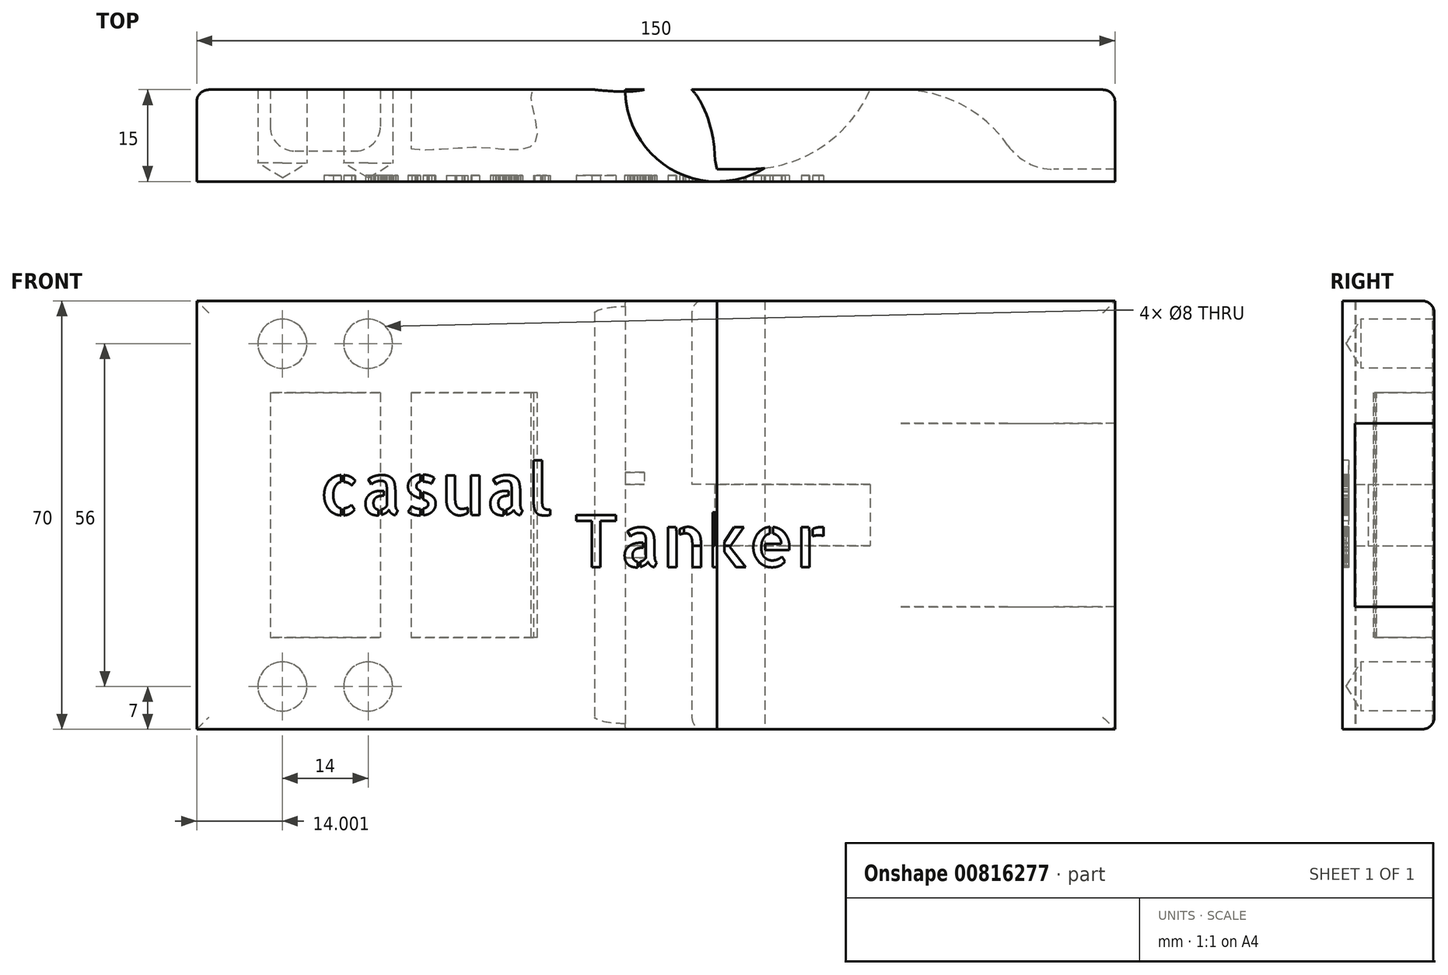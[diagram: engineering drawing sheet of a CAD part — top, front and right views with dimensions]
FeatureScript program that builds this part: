
annotation { "Feature Type Name" : "Feature", "Feature Type Description" : "" }
export const myFeature = defineFeature(function(context is Context, id is Id, definition is map)
    precondition{}
    {
        {
            var Q0;
            Q0=qCreatedBy(makeId("Top.planeOp"),FACE);
            var sketch = newSketch(context, id + "F0", { "sketchPlane" : qUnion([Q0])});
            skLineSegment(sketch, "E0.bottom", {"start": v(91.44, -7.74) * mm, "end": v(-58.56, -7.74) * mm});
            skLineSegment(sketch, "E0.top", {"start": v(91.44, 7.26) * mm, "end": v(-58.56, 7.26) * mm});
            skLineSegment(sketch, "E0.left", {"start": v(91.44, -7.74) * mm, "end": v(91.44, 7.26) * mm});
            skLineSegment(sketch, "E0.right", {"start": v(-58.56, -7.74) * mm, "end": v(-58.56, 7.26) * mm});
            skLineSegment(sketch, "E1", {"start": v(91.44, -5.74) * mm, "end": v(81.44, -5.74) * mm});
            skArc(sketch, "E2", {"start": v(81.44, -5.74) * mm, "mid": v(77.21, -4.7) * mm, "end": v(73.94, -1.84) * mm});
            skArc(sketch, "E3", {"start": v(73.94, -1.84) * mm, "mid": v(66.3, 4.85) * mm, "end": v(56.44, 7.26) * mm});
            skLineSegment(sketch, "E4", {"start": v(26.44, -5.74) * mm, "end": v(31.44, -5.74) * mm});
            skArc(sketch, "E5", {"start": v(31.44, -5.74) * mm, "mid": v(43.37, -2.2) * mm, "end": v(51.44, 7.26) * mm});
            skLineSegment(sketch, "E6", {"start": v(-58.56, -5.74) * mm, "end": v(106.76, -5.74) * mm, "construction": true});
            skFitSpline(sketch, "E7", {"points": [v(26.44, -5.74) * mm, v(25.26, -0.18) * mm, v(21.4, 5.71) * mm, v(6.44, 7.26) * mm], "startDerivative": vector(-4.01, 21.25) * mm, "endDerivative": vector(-55.89, 0) * mm});
            skLineSegment(sketch, "E8.bottom", {"start": v(-46.56, 7.26) * mm, "end": v(-28.56, 7.26) * mm});
            skLineSegment(sketch, "E8.top", {"start": v(-42.56, -2.74) * mm, "end": v(-32.56, -2.74) * mm});
            skLineSegment(sketch, "E8.left", {"start": v(-46.56, 7.26) * mm, "end": v(-46.56, 1.26) * mm});
            skLineSegment(sketch, "E8.right", {"start": v(-28.56, 7.26) * mm, "end": v(-28.56, 1.26) * mm});
            skLineSegment(sketch, "E9", {"start": v(-23.56, 7.26) * mm, "end": v(-23.56, -2.34) * mm});
            skFitSpline(sketch, "E10", {"points": [v(-23.56, -2.34) * mm, v(-16.77, -2.34) * mm, v(-10.45, -2.1) * mm, v(-4.83, 0) * mm, v(-3.56, 7.26) * mm], "startDerivative": vector(19.96, -2.18) * mm, "endDerivative": vector(3.98, 19.09) * mm});
            skPoint(sketch, "E11.visualSharp", {"position": v(-46.56, -2.74) * mm});
            skArc(sketch, "E11.filletArc", {"start": v(-46.56, 1.26) * mm, "mid": v(-45.39, -1.56) * mm, "end": v(-42.56, -2.74) * mm});
            skPoint(sketch, "E12.visualSharp", {"position": v(-28.56, -2.74) * mm});
            skArc(sketch, "E12.filletArc", {"start": v(-32.56, -2.74) * mm, "mid": v(-29.73, -1.56) * mm, "end": v(-28.56, 1.26) * mm});
            skCircle(sketch, "E13", {"center": v(26.44, 7.26) * mm, "radius": 15 * mm});
            skSolve(sketch);
        }
        {
            var Q0;
            Q0=qCreatedBy(makeId("Top.planeOp"),FACE);
            var sketch = newSketch(context, id + "F1", { "sketchPlane" : qUnion([Q0])});
            skFitSpline(sketch, "E14.0", {"points": [v(-23.56, -2.34) * mm, v(-21.87, -2.52) * mm, v(-16.45, -2.3) * mm, v(-10.78, -2.22) * mm, v(-3.3, -1.43) * mm, v(-3.9, 5.58) * mm, v(-3.56, 7.26) * mm]});
            skLineSegment(sketch, "E14.1", {"start": v(-23.56, 7.26) * mm, "end": v(-23.56, -2.34) * mm});
            skLineSegment(sketch, "E14.2", {"start": v(-28.56, 7.26) * mm, "end": v(-28.56, 1.26) * mm});
            skArc(sketch, "E14.3", {"start": v(-32.56, -2.74) * mm, "mid": v(-29.73, -1.56) * mm, "end": v(-28.56, 1.26) * mm});
            skLineSegment(sketch, "E14.4", {"start": v(-42.56, -2.74) * mm, "end": v(-32.56, -2.74) * mm});
            skArc(sketch, "E14.5", {"start": v(-46.56, 1.26) * mm, "mid": v(-45.39, -1.56) * mm, "end": v(-42.56, -2.74) * mm});
            skLineSegment(sketch, "E14.6", {"start": v(-46.56, 7.26) * mm, "end": v(-46.56, 1.26) * mm});
            skLineSegment(sketch, "E14.8", {"start": v(-58.56, -7.74) * mm, "end": v(-58.56, 7.26) * mm});
            skLineSegment(sketch, "E15", {"start": v(-58.56, -7.74) * mm, "end": v(1.44, -7.74) * mm});
            skLineSegment(sketch, "E16", {"start": v(1.44, 7.26) * mm, "end": v(-58.56, 7.26) * mm});
            skPoint(sketch, "E17.middle", {"position": v(1.44, 0) * mm});
            skFitSpline(sketch, "E18.0", {"points": [v(26.44, -5.74) * mm, v(26.08, -3.84) * mm, v(25.69, -0.2) * mm, v(21.45, 7.91) * mm, v(14.55, 7.26) * mm, v(6.44, 7.26) * mm]});
            skArc(sketch, "E18.1", {"start": v(31.44, -5.74) * mm, "mid": v(43.37, -2.2) * mm, "end": v(51.44, 7.26) * mm});
            skLineSegment(sketch, "E18.2", {"start": v(26.44, -5.74) * mm, "end": v(31.44, -5.74) * mm});
            skArc(sketch, "E18.3", {"start": v(73.94, -1.84) * mm, "mid": v(66.3, 4.85) * mm, "end": v(56.44, 7.26) * mm});
            skArc(sketch, "E18.4", {"start": v(81.44, -5.74) * mm, "mid": v(77.21, -4.7) * mm, "end": v(73.94, -1.84) * mm});
            skLineSegment(sketch, "E18.5", {"start": v(91.44, -5.74) * mm, "end": v(81.44, -5.74) * mm});
            skCircle(sketch, "E18.7", {"center": v(26.44, 7.26) * mm, "radius": 15 * mm});
            skLineSegment(sketch, "E19.bottom", {"start": v(1.44, 7.26) * mm, "end": v(91.44, 7.26) * mm});
            skLineSegment(sketch, "E19.top", {"start": v(1.44, -7.74) * mm, "end": v(91.44, -7.74) * mm});
            skLineSegment(sketch, "E19.right", {"start": v(91.44, 7.26) * mm, "end": v(91.44, -7.74) * mm});
            skSolve(sketch);
        }
        {
            var Q0;
            {var subQ5=sQuery(id+"F1.wireOp",EDGE,"E17.right");Q0=makeQuery(id+"F1.imprint","IMPRINT",FACE,{"disambiguationData":[TD([[makeQuery(id+"F1.imprint","IMPRINT",EDGE,{"derivedFrom":subQ5}),-1.0]])]});}
            var Q1;
            {var subQ6=sQuery(id+"F1.wireOp",EDGE,"E14.0");Q1=makeQuery(id+"F1.imprint","IMPRINT",FACE,{"disambiguationData":[TD([[makeQuery(id+"F1.imprint","IMPRINT",EDGE,{"derivedFrom":subQ6}),-1.0]])]});}
            var Q2;
            {var subQ0=sQuery(id+"F1.wireOp",EDGE,"E14.0");Q2=makeQuery(id+"F1.imprint","IMPRINT",FACE,{"disambiguationData":[TD([[makeQuery(id+"F1.imprint","IMPRINT",EDGE,{"derivedFrom":subQ0}),1.0]])]});}
            var Q3;
            {var subQ1=sQuery(id+"F1.wireOp",EDGE,"E14.2");Q3=makeQuery(id+"F1.imprint","IMPRINT",FACE,{"disambiguationData":[TD([[makeQuery(id+"F1.imprint","IMPRINT",EDGE,{"derivedFrom":subQ1}),-1.0]])]});}
            var Q4;
            {var subQ5=sQuery(id+"F1.wireOp",EDGE,"bb9fbce9-dafe-4efa-a9e3-36aaa79ced1d.1");Q4=makeQuery(id+"F1.imprint","IMPRINT",FACE,{"disambiguationData":[TD([[makeQuery(id+"F1.imprint","IMPRINT",EDGE,{"derivedFrom":subQ5}),-1.0]])]});}
            var Q5;
            {var subQ1=sQuery(id+"F1.wireOp",EDGE,"E14.1");Q5=makeQuery(id+"F1.imprint","IMPRINT",FACE,{"disambiguationData":[TD([[makeQuery(id+"F1.imprint","IMPRINT",EDGE,{"derivedFrom":subQ1}),-1.0]])]});}
            var Q6;
            {var subQ1=sQuery(id+"F1.wireOp",EDGE,"bb9fbce9-dafe-4efa-a9e3-36aaa79ced1d.1");var subQ3=sQuery(id+"F1.wireOp",EDGE,"E14.0");var subQ4=makeQuery(id+"F1.imprint","INTERSECT",VERTEX,{"derivedFrom":[subQ3,subQ1]});Q6=makeQuery(id+"F1.imprint","IMPRINT",FACE,{"disambiguationData":[TD([[makeQuery(id+"F1.imprint","IMPRINT",EDGE,{"disambiguationData":[TD([[subQ4,-1.0]])],"derivedFrom":subQ3}),-1.0]])]});}
            extrude(context, id + "F2", {"entities" : qUnion([Q0, Q1, Q2, Q3, Q4, Q5, Q6]), "depth" : 70 * mm, "offsetDistance" : 25 * mm, "symmetric" : true});
        }
        {
            var Q0;
            {var subQ1=sQuery(id+"F1.wireOp",EDGE,"E14.2");Q0=makeQuery(id+"F1.imprint","IMPRINT",FACE,{"disambiguationData":[TD([[makeQuery(id+"F1.imprint","IMPRINT",EDGE,{"derivedFrom":subQ1}),-1.0]])]});}
            var Q1;
            {var subQ0=sQuery(id+"F1.wireOp",EDGE,"E14.0");Q1=makeQuery(id+"F1.imprint","IMPRINT",FACE,{"disambiguationData":[TD([[makeQuery(id+"F1.imprint","IMPRINT",EDGE,{"derivedFrom":subQ0}),1.0]])]});}
            extrude(context, id + "F3", {"entities" : qUnion([Q0, Q1]), "operationType" : NewBodyOperationType.REMOVE, "depth" : 40 * mm, "offsetDistance" : 25 * mm, "symmetric" : true});
        }
        {
            var Q0;
            {var subQ4=sQuery(id+"F1.wireOp",EDGE,"E17.left");Q0=makeQuery(id+"F1.imprint","IMPRINT",FACE,{"disambiguationData":[TD([[makeQuery(id+"F1.imprint","IMPRINT",EDGE,{"derivedFrom":subQ4}),-1.0]])]});}
            var Q1;
            {var subQ0=sQuery(id+"F1.wireOp",EDGE,"E17.left");Q1=makeQuery(id+"F1.imprint","IMPRINT",FACE,{"disambiguationData":[TD([[makeQuery(id+"F1.imprint","IMPRINT",EDGE,{"derivedFrom":subQ0}),1.0]])]});}
            var Q2;
            {var subQ4=sQuery(id+"F1.wireOp",EDGE,"E18.3");Q2=makeQuery(id+"F1.imprint","IMPRINT",FACE,{"disambiguationData":[TD([[makeQuery(id+"F1.imprint","IMPRINT",EDGE,{"derivedFrom":subQ4}),1.0]])]});}
            var Q3;
            {var subQ1=sQuery(id+"F1.wireOp",EDGE,"E18.3");Q3=makeQuery(id+"F1.imprint","IMPRINT",FACE,{"disambiguationData":[TD([[makeQuery(id+"F1.imprint","IMPRINT",EDGE,{"derivedFrom":subQ1}),-1.0]])]});}
            var Q4;
            {var subQ0=sQuery(id+"F1.wireOp",EDGE,"E19.bottom");var subQ1=sQuery(id+"F1.wireOp",EDGE,"E18.1");var subQ2=makeQuery(id+"F1.imprint","INTERSECT",VERTEX,{"derivedFrom":[subQ1,subQ0]});Q4=makeQuery(id+"F1.imprint","IMPRINT",FACE,{"disambiguationData":[TD([[makeQuery(id+"F1.imprint","IMPRINT",EDGE,{"disambiguationData":[TD([[subQ2,1.0]])],"derivedFrom":subQ1}),1.0]])]});}
            var Q5;
            {var subQ4=sQuery(id+"F1.wireOp",EDGE,"E18.2");Q5=makeQuery(id+"F1.imprint","IMPRINT",FACE,{"disambiguationData":[TD([[makeQuery(id+"F1.imprint","IMPRINT",EDGE,{"derivedFrom":subQ4}),-1.0]])]});}
            var Q6;
            {var subQ5=sQuery(id+"F1.wireOp",EDGE,"E18.2");Q6=makeQuery(id+"F1.imprint","IMPRINT",FACE,{"disambiguationData":[TD([[makeQuery(id+"F1.imprint","IMPRINT",EDGE,{"derivedFrom":subQ5}),1.0]])]});}
            extrude(context, id + "F4", {"entities" : qUnion([Q0, Q1, Q2, Q3, Q4, Q5, Q6]), "operationType" : NewBodyOperationType.ADD, "depth" : 70 * mm, "offsetDistance" : 25 * mm, "symmetric" : true});
        }
        {
            var Q0;
            {var subQ0=sQuery(id+"F1.wireOp",EDGE,"E18.7");var subQ1=sQuery(id+"F1.wireOp",EDGE,"E18.0");var subQ2=makeQuery(id+"F1.imprint","INTERSECT",VERTEX,{"derivedFrom":[subQ1,subQ0]});Q0=makeQuery(id+"F1.imprint","IMPRINT",FACE,{"disambiguationData":[TD([[makeQuery(id+"F1.imprint","IMPRINT",EDGE,{"disambiguationData":[TD([[subQ2,1.0]])],"derivedFrom":subQ1}),-1.0]])]});}
            extrude(context, id + "F5", {"entities" : qUnion([Q0]), "operationType" : NewBodyOperationType.ADD, "depth" : 14 * mm, "offsetDistance" : 25 * mm, "symmetric" : true});
        }
        {
            var Q0;
            {var subQ0=sQuery(id+"F1.wireOp",EDGE,"E18.7");var subQ1=sQuery(id+"F1.wireOp",EDGE,"E18.0");var subQ2=makeQuery(id+"F1.imprint","INTERSECT",VERTEX,{"disambiguationData":[OD(0.0)],"derivedFrom":[subQ1,subQ0]});Q0=makeQuery(id+"F1.imprint","IMPRINT",FACE,{"disambiguationData":[TD([[makeQuery(id+"F1.imprint","IMPRINT",EDGE,{"disambiguationData":[TD([[subQ2,1.0]])],"derivedFrom":subQ1}),-1.0]])]});}
            var Q1;
            {var subQ1=sQuery(id+"F0.wireOp",EDGE,"E4");Q1=makeQuery(id+"F0.imprint","IMPRINT",FACE,{"disambiguationData":[TD([[makeQuery(id+"F0.imprint","IMPRINT",EDGE,{"derivedFrom":subQ1}),1.0]])]});}
            var Q2;
            {var subQ0=sQuery(id+"F0.wireOp",EDGE,"E5");var subQ1=sQuery(id+"F0.wireOp",EDGE,"E0.top");var subQ2=makeQuery(id+"F0.imprint","INTERSECT",VERTEX,{"derivedFrom":[subQ1,subQ0]});Q2=makeQuery(id+"F0.imprint","IMPRINT",FACE,{"disambiguationData":[TD([[makeQuery(id+"F0.imprint","IMPRINT",EDGE,{"disambiguationData":[TD([[subQ2,-1.0]])],"derivedFrom":subQ1}),1.0]])]});}
            extrude(context, id + "F6", {"entities" : qUnion([Q0, Q1, Q2]), "operationType" : NewBodyOperationType.REMOVE, "depth" : 10 * mm, "offsetDistance" : 25 * mm, "symmetric" : true});
        }
        {
            var Q0;
            {var subQ0=sQuery(id+"F1.wireOp",EDGE,"E18.7");var subQ1=sQuery(id+"F1.wireOp",EDGE,"E18.0");var subQ2=makeQuery(id+"F1.imprint","INTERSECT",VERTEX,{"disambiguationData":[OD(1.0)],"derivedFrom":[subQ1,subQ0]});Q0=makeQuery(id+"F1.imprint","IMPRINT",FACE,{"disambiguationData":[TD([[makeQuery(id+"F1.imprint","IMPRINT",EDGE,{"disambiguationData":[TD([[subQ2,-1.0]])],"derivedFrom":subQ1}),-1.0]])]});}
            var Q1;
            {var subQ5=sQuery(id+"F1.wireOp",EDGE,"E18.1");Q1=makeQuery(id+"F1.imprint","IMPRINT",FACE,{"disambiguationData":[TD([[makeQuery(id+"F1.imprint","IMPRINT",EDGE,{"derivedFrom":subQ5}),1.0]])]});}
            extrude(context, id + "F7", {"entities" : qUnion([Q0, Q1]), "operationType" : NewBodyOperationType.REMOVE, "oppositeDirection" : true, "depth" : 10 * mm, "offsetDistance" : 25 * mm, "symmetric" : true});
        }
        {
            var Q0;
            {var subQ1=sQuery(id+"F1.wireOp",EDGE,"E18.3");Q0=makeQuery(id+"F1.imprint","IMPRINT",FACE,{"disambiguationData":[TD([[makeQuery(id+"F1.imprint","IMPRINT",EDGE,{"derivedFrom":subQ1}),-1.0]])]});}
            extrude(context, id + "F8", {"entities" : qUnion([Q0]), "operationType" : NewBodyOperationType.REMOVE, "depth" : 30 * mm, "offsetDistance" : 25 * mm, "symmetric" : true});
        }
        {
            var Q0;
            {var subQ0=sQuery(id+"F1.wireOp",EDGE,"E19.bottom");var subQ1=makeQuery(id+"F1.imprint","INTERSECT",VERTEX,{"derivedFrom":[sQuery(id+"F1.wireOp",EDGE,"E18.3"),subQ0]});var subQ2=makeQuery(id+"F1.imprint","INTERSECT",VERTEX,{"derivedFrom":[sQuery(id+"F1.wireOp",EDGE,"E18.1"),subQ0]});var subQ3=sQuery(id+"F1.wireOp",EDGE,"E18.7");var subQ4=makeQuery(id+"F1.imprint","INTERSECT",VERTEX,{"disambiguationData":[OD(0.0)],"derivedFrom":[subQ3,subQ0]});var subQ5=sQuery(id+"F1.wireOp",EDGE,"E18.0");var subQ6=makeQuery(id+"F1.imprint","INTERSECT",VERTEX,{"disambiguationData":[OD(1.0)],"derivedFrom":[subQ5,subQ0]});var subQ8=makeQuery(id+"F1.imprint","INTERSECT",VERTEX,{"disambiguationData":[OD(0.0)],"derivedFrom":[subQ5,subQ0]});Q0=makeQuery(id+"Fk8vee3glepebii_2.boolean.opBoolean","MERGE",EDGE,{"derivedFrom":[makeQuery(id+"F4.opExtrude","CAP_EDGE",EDGE,{"disambiguationData":[OSD([subQ0]),TDD([makeQuery(id+"F1.imprint","IMPRINT",EDGE,{"disambiguationData":[TD([[subQ8,1.0]])],"derivedFrom":subQ0}),makeQuery(id+"F1.imprint","IMPRINT",EDGE,{"disambiguationData":[TD([[subQ8,-1.0]])],"derivedFrom":subQ0})])],"isStart":false}),makeQuery(id+"F4.opExtrude","CAP_EDGE",EDGE,{"disambiguationData":[OSD([subQ0]),TDD([makeQuery(id+"F1.imprint","IMPRINT",EDGE,{"disambiguationData":[TD([[subQ2,-1.0]])],"derivedFrom":subQ0})])],"isStart":false}),makeQuery(id+"Fk8vee3glepebii_2.opExtrude","CAP_EDGE",EDGE,{"disambiguationData":[OSD([subQ0]),TDD([makeQuery(id+"F1.imprint","IMPRINT",EDGE,{"disambiguationData":[TD([[subQ6,1.0]])],"derivedFrom":subQ0}),makeQuery(id+"F1.imprint","IMPRINT",EDGE,{"disambiguationData":[TD([[subQ4,1.0]])],"derivedFrom":subQ0}),makeQuery(id+"F1.imprint","IMPRINT",EDGE,{"disambiguationData":[TD([[subQ2,1.0]])],"derivedFrom":subQ0})])],"isStart":false}),makeQuery(id+"Fk8vee3glepebii_2.opExtrude","CAP_EDGE",EDGE,{"disambiguationData":[OSD([subQ0]),TDD([makeQuery(id+"F1.imprint","IMPRINT",EDGE,{"disambiguationData":[TD([[subQ1,-1.0]])],"derivedFrom":subQ0})])],"isStart":false})]});}
            var Q1;
            {var subQ0=sQuery(id+"F1.wireOp",EDGE,"E19.bottom");var subQ3=sQuery(id+"F1.wireOp",EDGE,"E19.right");var subQ4=sQuery(id+"F1.wireOp",EDGE,"E18.1");var subQ6=sQuery(id+"F1.wireOp",EDGE,"E18.7");var subQ8=sQuery(id+"F1.wireOp",EDGE,"E18.0");var subQ13=sQuery(id+"F1.wireOp",EDGE,"E18.2");Q1=makeQuery(id+"F8.boolean.opBoolean","SPLIT",EDGE,{"disambiguationData":[TD([makeQuery(id+"Fk8vee3glepebii_2.opExtrude","CAP_FACE",FACE,{"disambiguationData":[OSD([subQ8,subQ4,subQ13,subQ6,subQ0])],"isStart":false})])],"derivedFrom":makeQuery(id+"Fk8vee3glepebii_2.opExtrude","SWEPT_EDGE",EDGE,{"disambiguationData":[OSD([subQ0,subQ3])]})});}
            var Q2;
            {var subQ0=sQuery(id+"F1.wireOp",EDGE,"E19.right");var subQ1=sQuery(id+"F1.wireOp",EDGE,"E19.bottom");var subQ2=sQuery(id+"F1.wireOp",EDGE,"E18.1");var subQ4=sQuery(id+"F1.wireOp",EDGE,"E18.7");var subQ6=sQuery(id+"F1.wireOp",EDGE,"E18.0");var subQ11=sQuery(id+"F1.wireOp",EDGE,"E18.2");Q2=makeQuery(id+"F8.boolean.opBoolean","SPLIT",EDGE,{"disambiguationData":[TD([makeQuery(id+"Fk8vee3glepebii_2.opExtrude","CAP_FACE",FACE,{"disambiguationData":[OSD([subQ6,subQ2,subQ11,subQ4,subQ1])],"isStart":true})])],"derivedFrom":makeQuery(id+"Fk8vee3glepebii_2.opExtrude","SWEPT_EDGE",EDGE,{"disambiguationData":[OSD([subQ1,subQ0])]})});}
            var Q3;
            {var subQ0=sQuery(id+"F1.wireOp",EDGE,"E19.bottom");var subQ1=makeQuery(id+"F1.imprint","INTERSECT",VERTEX,{"derivedFrom":[sQuery(id+"F1.wireOp",EDGE,"E18.3"),subQ0]});var subQ2=makeQuery(id+"F1.imprint","INTERSECT",VERTEX,{"derivedFrom":[sQuery(id+"F1.wireOp",EDGE,"E18.1"),subQ0]});var subQ3=sQuery(id+"F1.wireOp",EDGE,"E18.7");var subQ4=makeQuery(id+"F1.imprint","INTERSECT",VERTEX,{"disambiguationData":[OD(0.0)],"derivedFrom":[subQ3,subQ0]});var subQ5=sQuery(id+"F1.wireOp",EDGE,"E18.0");var subQ6=makeQuery(id+"F1.imprint","INTERSECT",VERTEX,{"disambiguationData":[OD(1.0)],"derivedFrom":[subQ5,subQ0]});var subQ8=makeQuery(id+"F1.imprint","INTERSECT",VERTEX,{"disambiguationData":[OD(0.0)],"derivedFrom":[subQ5,subQ0]});Q3=makeQuery(id+"Fk8vee3glepebii_2.boolean.opBoolean","MERGE",EDGE,{"derivedFrom":[makeQuery(id+"F4.opExtrude","CAP_EDGE",EDGE,{"disambiguationData":[OSD([subQ0]),TDD([makeQuery(id+"F1.imprint","IMPRINT",EDGE,{"disambiguationData":[TD([[subQ8,1.0]])],"derivedFrom":subQ0}),makeQuery(id+"F1.imprint","IMPRINT",EDGE,{"disambiguationData":[TD([[subQ8,-1.0]])],"derivedFrom":subQ0})])],"isStart":true}),makeQuery(id+"F4.opExtrude","CAP_EDGE",EDGE,{"disambiguationData":[OSD([subQ0]),TDD([makeQuery(id+"F1.imprint","IMPRINT",EDGE,{"disambiguationData":[TD([[subQ2,-1.0]])],"derivedFrom":subQ0})])],"isStart":true}),makeQuery(id+"Fk8vee3glepebii_2.opExtrude","CAP_EDGE",EDGE,{"disambiguationData":[OSD([subQ0]),TDD([makeQuery(id+"F1.imprint","IMPRINT",EDGE,{"disambiguationData":[TD([[subQ6,1.0]])],"derivedFrom":subQ0}),makeQuery(id+"F1.imprint","IMPRINT",EDGE,{"disambiguationData":[TD([[subQ4,1.0]])],"derivedFrom":subQ0}),makeQuery(id+"F1.imprint","IMPRINT",EDGE,{"disambiguationData":[TD([[subQ2,1.0]])],"derivedFrom":subQ0})])],"isStart":true}),makeQuery(id+"Fk8vee3glepebii_2.opExtrude","CAP_EDGE",EDGE,{"disambiguationData":[OSD([subQ0]),TDD([makeQuery(id+"F1.imprint","IMPRINT",EDGE,{"disambiguationData":[TD([[subQ1,-1.0]])],"derivedFrom":subQ0})])],"isStart":true})]});}
            var Q4;
            Q4=makeQuery(id+"F2.opExtrude","CAP_EDGE",EDGE,{"disambiguationData":[OSD([sQuery(id+"F1.wireOp",EDGE,"E16")])],"isStart":false});
            var Q5;
            Q5=makeQuery(id+"F2.opExtrude","SWEPT_EDGE",EDGE,{"disambiguationData":[OSD([sQuery(id+"F1.wireOp",EDGE,"E14.8"),sQuery(id+"F1.wireOp",EDGE,"E16")])]});
            var Q6;
            Q6=makeQuery(id+"F2.opExtrude","CAP_EDGE",EDGE,{"disambiguationData":[OSD([sQuery(id+"F1.wireOp",EDGE,"E16")])],"isStart":true});
            var Q7;
            Q7=makeQuery(id+"F3.boolean.opBoolean","COPY",EDGE,{"derivedFrom":makeQuery(id+"F3.opExtrude","SWEPT_EDGE",EDGE,{"disambiguationData":[OSD([sQuery(id+"F1.wireOp",EDGE,"E14.6"),sQuery(id+"F1.wireOp",EDGE,"E16")])]})});
            var Q8;
            Q8=makeQuery(id+"F3.boolean.opBoolean","COPY",EDGE,{"derivedFrom":makeQuery(id+"F3.opExtrude","SWEPT_EDGE",EDGE,{"disambiguationData":[OSD([sQuery(id+"F1.wireOp",EDGE,"E14.2"),sQuery(id+"F1.wireOp",EDGE,"E16")])]})});
            var Q9;
            Q9=makeQuery(id+"F3.boolean.opBoolean","COPY",EDGE,{"derivedFrom":makeQuery(id+"F3.opExtrude","SWEPT_EDGE",EDGE,{"disambiguationData":[OSD([sQuery(id+"F1.wireOp",EDGE,"E14.1"),sQuery(id+"F1.wireOp",EDGE,"E16")])]})});
            var Q10;
            {var subQ0=sQuery(id+"F1.wireOp",EDGE,"E16");Q10=makeQuery(id+"F3.boolean.opBoolean","COPY",EDGE,{"derivedFrom":makeQuery(id+"F3.opExtrude","CAP_EDGE",EDGE,{"disambiguationData":[OSD([subQ0]),TDD([makeQuery(id+"F1.imprint","IMPRINT",EDGE,{"disambiguationData":[TD([[makeQuery(id+"F1.imprint","INTERSECT",VERTEX,{"derivedFrom":[sQuery(id+"F1.wireOp",EDGE,"E14.2"),subQ0]}),-1.0]])],"derivedFrom":subQ0})])],"isStart":true})});}
            var Q11;
            {var subQ0=sQuery(id+"F1.wireOp",EDGE,"E16");Q11=makeQuery(id+"F3.boolean.opBoolean","COPY",EDGE,{"derivedFrom":makeQuery(id+"F3.opExtrude","CAP_EDGE",EDGE,{"disambiguationData":[OSD([subQ0]),TDD([makeQuery(id+"F1.imprint","IMPRINT",EDGE,{"disambiguationData":[TD([[makeQuery(id+"F1.imprint","INTERSECT",VERTEX,{"derivedFrom":[sQuery(id+"F1.wireOp",EDGE,"E14.2"),subQ0]}),-1.0]])],"derivedFrom":subQ0})])],"isStart":false})});}
            var Q12;
            {var subQ0=sQuery(id+"F1.wireOp",EDGE,"E19.bottom");var subQ2=sQuery(id+"F1.wireOp",EDGE,"E19.right");var subQ3=sQuery(id+"F1.wireOp",EDGE,"E19.top");var subQ4=sQuery(id+"F1.wireOp",EDGE,"E18.7");Q12=makeQuery(id+"F8.boolean.opBoolean","SPLIT",EDGE,{"disambiguationData":[TD([makeQuery(id+"F4.opExtrude","CAP_FACE",FACE,{"disambiguationData":[OSD([subQ4,subQ0,subQ3,subQ2])],"isStart":false})])],"derivedFrom":makeQuery(id+"F4.opExtrude","SWEPT_EDGE",EDGE,{"disambiguationData":[OSD([subQ0,subQ2])]})});}
            var Q13;
            {var subQ0=sQuery(id+"F1.wireOp",EDGE,"E19.right");var subQ1=sQuery(id+"F1.wireOp",EDGE,"E19.top");var subQ2=sQuery(id+"F1.wireOp",EDGE,"E19.bottom");var subQ3=sQuery(id+"F1.wireOp",EDGE,"E18.7");Q13=makeQuery(id+"F8.boolean.opBoolean","SPLIT",EDGE,{"disambiguationData":[TD([makeQuery(id+"F4.opExtrude","CAP_FACE",FACE,{"disambiguationData":[OSD([subQ3,subQ2,subQ1,subQ0])],"isStart":true})])],"derivedFrom":makeQuery(id+"F4.opExtrude","SWEPT_EDGE",EDGE,{"disambiguationData":[OSD([subQ2,subQ0])]})});}
            fillet(context, id + "F9", {"entities" : qUnion([Q0, Q1, Q2, Q3, Q4, Q5, Q6, Q7, Q8, Q9, Q10, Q11, Q12, Q13]), "radius" : 2 * mm, "tangentPropagation" : true, "allowEdgeOverflow" : false});
        }
        {
            var Q0;
            {var subQ0=sQuery(id+"F1.wireOp",EDGE,"E19.top");Q0=makeQuery(id+"F4.boolean.opBoolean","MERGE",FACE,{"derivedFrom":[makeQuery(id+"F2.opExtrude","SWEPT_FACE",FACE,{"disambiguationData":[OSD([sQuery(id+"F1.wireOp",EDGE,"E15"),subQ0])]}),makeQuery(id+"F4.opExtrude","SWEPT_FACE",FACE,{"disambiguationData":[OSD([subQ0])]})]});}
            var sketch = newSketch(context, id + "F10", { "sketchPlane" : qUnion([Q0])});
            skText(sketch, "E20", { "text": "casual", "fontName": "AllertaStencil-Regular.ttf"});
            skText(sketch, "E21", { "text": "Tanker", "fontName": "AllertaStencil-Regular.ttf"});
            skLineSegment(sketch, "E22", {"start": v(-53.13, 0) * mm, "end": v(83.14, 0) * mm, "construction": true});
            skPoint(sketch, "E23.0", {"position": v(0, 0) * mm});
            const initialGuessF10  = {"E20": [-0.03855, 0, 1, 0, 0.0085], "E21": [0.00288, -0.0085, 1, 0, 0.0085]};
            skSetInitialGuess(sketch, initialGuessF10);
            skSolve(sketch);
        }
        {
            var Q0;
            Q0=makeQuery(id+"F10.imprint","IMPRINT",FACE,{"disambiguationData":[TD([[makeQuery(id+"F10.imprint","IMPRINT",EDGE,{"derivedFrom":sQuery(id+"F10.wireOp",EDGE,"E20.sketch_text.stroke-11")}),-1.0]])]});
            var Q1;
            Q1=makeQuery(id+"F10.imprint","IMPRINT",FACE,{"disambiguationData":[TD([[makeQuery(id+"F10.imprint","IMPRINT",EDGE,{"derivedFrom":sQuery(id+"F10.wireOp",EDGE,"E20.sketch_text.stroke-0")}),-1.0]])]});
            var Q2;
            Q2=makeQuery(id+"F10.imprint","IMPRINT",FACE,{"disambiguationData":[TD([[makeQuery(id+"F10.imprint","IMPRINT",EDGE,{"derivedFrom":sQuery(id+"F10.wireOp",EDGE,"E20.sketch_text.stroke-5")}),-1.0]])]});
            var Q3;
            Q3=makeQuery(id+"F10.imprint","IMPRINT",FACE,{"disambiguationData":[TD([[makeQuery(id+"F10.imprint","IMPRINT",EDGE,{"derivedFrom":sQuery(id+"F10.wireOp",EDGE,"E20.sketch_text.stroke-29")}),-1.0]])]});
            var Q4;
            Q4=makeQuery(id+"F10.imprint","IMPRINT",FACE,{"disambiguationData":[TD([[makeQuery(id+"F10.imprint","IMPRINT",EDGE,{"derivedFrom":sQuery(id+"F10.wireOp",EDGE,"E20.sketch_text.stroke-48")}),-1.0]])]});
            var Q5;
            Q5=makeQuery(id+"F10.imprint","IMPRINT",FACE,{"disambiguationData":[TD([[makeQuery(id+"F10.imprint","IMPRINT",EDGE,{"derivedFrom":sQuery(id+"F10.wireOp",EDGE,"E20.sketch_text.stroke-84")}),-1.0]])]});
            var Q6;
            Q6=makeQuery(id+"F10.imprint","IMPRINT",FACE,{"disambiguationData":[TD([[makeQuery(id+"F10.imprint","IMPRINT",EDGE,{"derivedFrom":sQuery(id+"F10.wireOp",EDGE,"E20.sketch_text.stroke-98")}),-1.0]])]});
            var Q7;
            Q7=makeQuery(id+"F10.imprint","IMPRINT",FACE,{"disambiguationData":[TD([[makeQuery(id+"F10.imprint","IMPRINT",EDGE,{"derivedFrom":sQuery(id+"F10.wireOp",EDGE,"E20.sketch_text.stroke-113")}),-1.0]])]});
            var Q8;
            Q8=makeQuery(id+"F10.imprint","IMPRINT",FACE,{"disambiguationData":[TD([[makeQuery(id+"F10.imprint","IMPRINT",EDGE,{"derivedFrom":sQuery(id+"F10.wireOp",EDGE,"E20.sketch_text.stroke-104")}),-1.0]])]});
            var Q9;
            Q9=makeQuery(id+"F10.imprint","IMPRINT",FACE,{"disambiguationData":[TD([[makeQuery(id+"F10.imprint","IMPRINT",EDGE,{"derivedFrom":sQuery(id+"F10.wireOp",EDGE,"E20.sketch_text.stroke-127")}),-1.0]])]});
            var Q10;
            Q10=makeQuery(id+"F10.imprint","IMPRINT",FACE,{"disambiguationData":[TD([[makeQuery(id+"F10.imprint","IMPRINT",EDGE,{"derivedFrom":sQuery(id+"F10.wireOp",EDGE,"E20.sketch_text.stroke-147")}),-1.0]])]});
            var Q11;
            Q11=makeQuery(id+"F10.imprint","IMPRINT",FACE,{"disambiguationData":[TD([[makeQuery(id+"F10.imprint","IMPRINT",EDGE,{"derivedFrom":sQuery(id+"F10.wireOp",EDGE,"E20.sketch_text.stroke-152")}),-1.0]])]});
            var Q12;
            Q12=makeQuery(id+"F10.imprint","IMPRINT",FACE,{"disambiguationData":[TD([[makeQuery(id+"F10.imprint","IMPRINT",EDGE,{"derivedFrom":sQuery(id+"F10.wireOp",EDGE,"E20.sketch_text.stroke-171")}),-1.0]])]});
            var Q13;
            Q13=makeQuery(id+"F10.imprint","IMPRINT",FACE,{"disambiguationData":[TD([[makeQuery(id+"F10.imprint","IMPRINT",EDGE,{"derivedFrom":sQuery(id+"F10.wireOp",EDGE,"E20.sketch_text.stroke-207")}),-1.0]])]});
            var Q14;
            Q14=makeQuery(id+"F10.imprint","IMPRINT",FACE,{"disambiguationData":[TD([[makeQuery(id+"F10.imprint","IMPRINT",EDGE,{"derivedFrom":sQuery(id+"F10.wireOp",EDGE,"E20.sketch_text.stroke-12")}),-1.0]])]});
            extrude(context, id + "F11", {"entities" : qUnion([Q0, Q1, Q2, Q3, Q4, Q5, Q6, Q7, Q8, Q9, Q10, Q11, Q12, Q13, Q14]), "operationType" : NewBodyOperationType.REMOVE, "oppositeDirection" : true, "depth" : 1 * mm, "offsetDistance" : 25 * mm});
        }
        {
            var Q0;
            Q0=makeQuery(id+"F10.imprint","IMPRINT",FACE,{"disambiguationData":[TD([[makeQuery(id+"F10.imprint","IMPRINT",EDGE,{"derivedFrom":sQuery(id+"F10.wireOp",EDGE,"E21.sketch_text.stroke-0")}),-1.0]])]});
            var Q1;
            Q1=makeQuery(id+"F10.imprint","IMPRINT",FACE,{"disambiguationData":[TD([[makeQuery(id+"F10.imprint","IMPRINT",EDGE,{"derivedFrom":sQuery(id+"F10.wireOp",EDGE,"E21.sketch_text.stroke-8")}),-1.0]])]});
            var Q2;
            Q2=makeQuery(id+"F10.imprint","IMPRINT",FACE,{"disambiguationData":[TD([[makeQuery(id+"F10.imprint","IMPRINT",EDGE,{"derivedFrom":sQuery(id+"F10.wireOp",EDGE,"E21.sketch_text.stroke-27")}),-1.0]])]});
            var Q3;
            Q3=makeQuery(id+"F10.imprint","IMPRINT",FACE,{"disambiguationData":[TD([[makeQuery(id+"F10.imprint","IMPRINT",EDGE,{"derivedFrom":sQuery(id+"F10.wireOp",EDGE,"E21.sketch_text.stroke-63")}),-1.0]])]});
            var Q4;
            Q4=makeQuery(id+"F10.imprint","IMPRINT",FACE,{"disambiguationData":[TD([[makeQuery(id+"F10.imprint","IMPRINT",EDGE,{"derivedFrom":sQuery(id+"F10.wireOp",EDGE,"E21.sketch_text.stroke-68")}),-1.0]])]});
            var Q5;
            Q5=makeQuery(id+"F10.imprint","IMPRINT",FACE,{"disambiguationData":[TD([[makeQuery(id+"F10.imprint","IMPRINT",EDGE,{"derivedFrom":sQuery(id+"F10.wireOp",EDGE,"E21.sketch_text.stroke-94")}),-1.0]])]});
            var Q6;
            Q6=makeQuery(id+"F10.imprint","IMPRINT",FACE,{"disambiguationData":[TD([[makeQuery(id+"F10.imprint","IMPRINT",EDGE,{"derivedFrom":sQuery(id+"F10.wireOp",EDGE,"E21.sketch_text.stroke-87")}),-1.0]])]});
            var Q7;
            Q7=makeQuery(id+"F10.imprint","IMPRINT",FACE,{"disambiguationData":[TD([[makeQuery(id+"F10.imprint","IMPRINT",EDGE,{"derivedFrom":sQuery(id+"F10.wireOp",EDGE,"E21.sketch_text.stroke-111")}),-1.0]])]});
            var Q8;
            Q8=makeQuery(id+"F10.imprint","IMPRINT",FACE,{"disambiguationData":[TD([[makeQuery(id+"F10.imprint","IMPRINT",EDGE,{"derivedFrom":sQuery(id+"F10.wireOp",EDGE,"E21.sketch_text.stroke-98")}),-1.0]])]});
            var Q9;
            Q9=makeQuery(id+"F10.imprint","IMPRINT",FACE,{"disambiguationData":[TD([[makeQuery(id+"F10.imprint","IMPRINT",EDGE,{"derivedFrom":sQuery(id+"F10.wireOp",EDGE,"E21.sketch_text.stroke-135")}),-1.0]])]});
            var Q10;
            Q10=makeQuery(id+"F10.imprint","IMPRINT",FACE,{"disambiguationData":[TD([[makeQuery(id+"F10.imprint","IMPRINT",EDGE,{"derivedFrom":sQuery(id+"F10.wireOp",EDGE,"E21.sketch_text.stroke-142")}),-1.0]])]});
            extrude(context, id + "F12", {"entities" : qUnion([Q0, Q1, Q2, Q3, Q4, Q5, Q6, Q7, Q8, Q9, Q10]), "operationType" : NewBodyOperationType.REMOVE, "oppositeDirection" : true, "depth" : 1 * mm, "offsetDistance" : 25 * mm});
        }
        {
            var Q0;
            Q0=makeQuery(id+"F2.opExtrude","SWEPT_FACE",FACE,{"disambiguationData":[OSD([sQuery(id+"F1.wireOp",EDGE,"E16")])]});
            var sketch = newSketch(context, id + "F13", { "sketchPlane" : qUnion([Q0])});
            skPoint(sketch, "E24.MirrorP", {"position": v(37.6, 0.24) * mm});
            skPoint(sketch, "E25", {"position": v(44.56, -28) * mm});
            skPoint(sketch, "E26", {"position": v(30.56, -28) * mm});
            skPoint(sketch, "E27.MirrorP", {"position": v(30.56, 28) * mm});
            skPoint(sketch, "E28.MirrorP", {"position": v(44.56, 28) * mm});
            skSolve(sketch);
        }
        {
            var Q0;
            Q0=sQuery(id+"F13.wireOp",VERTEX,"E25");
            var Q1;
            Q1=sQuery(id+"F13.wireOp",VERTEX,"E26");
            var Q2;
            Q2=sQuery(id+"F13.wireOp",VERTEX,"E28.MirrorP");
            var Q3;
            Q3=sQuery(id+"F13.wireOp",VERTEX,"E27.MirrorP");
            var Q4;
            Q4=makeQuery(id+"F2.opExtrude","SWEPT_BODY",BODY,{"disambiguationData":[OSD([sQuery(id+"F1.wireOp",EDGE,"E14.8"),sQuery(id+"F1.wireOp",EDGE,"E15"),sQuery(id+"F1.wireOp",EDGE,"E16"),sQuery(id+"F1.wireOp",EDGE,"E19.left")])]});
            hole(context, id + "F14", {"style" : HoleStyle.SIMPLE, "endStyle" : HoleEndStyle.BLIND, "holeDiameter" : 8 * mm, "majorDiameter" : 5 * mm, "holeDepth" : 12 * mm, "isTappedThrough" : true, "tappedDepth" : 12 * mm, "tapClearance" : 3, "locations" : qUnion([Q0, Q1, Q2, Q3]), "scope" : qUnion([Q4]), "startStyle" : HoleStartStyle.PART});
        }
    });
